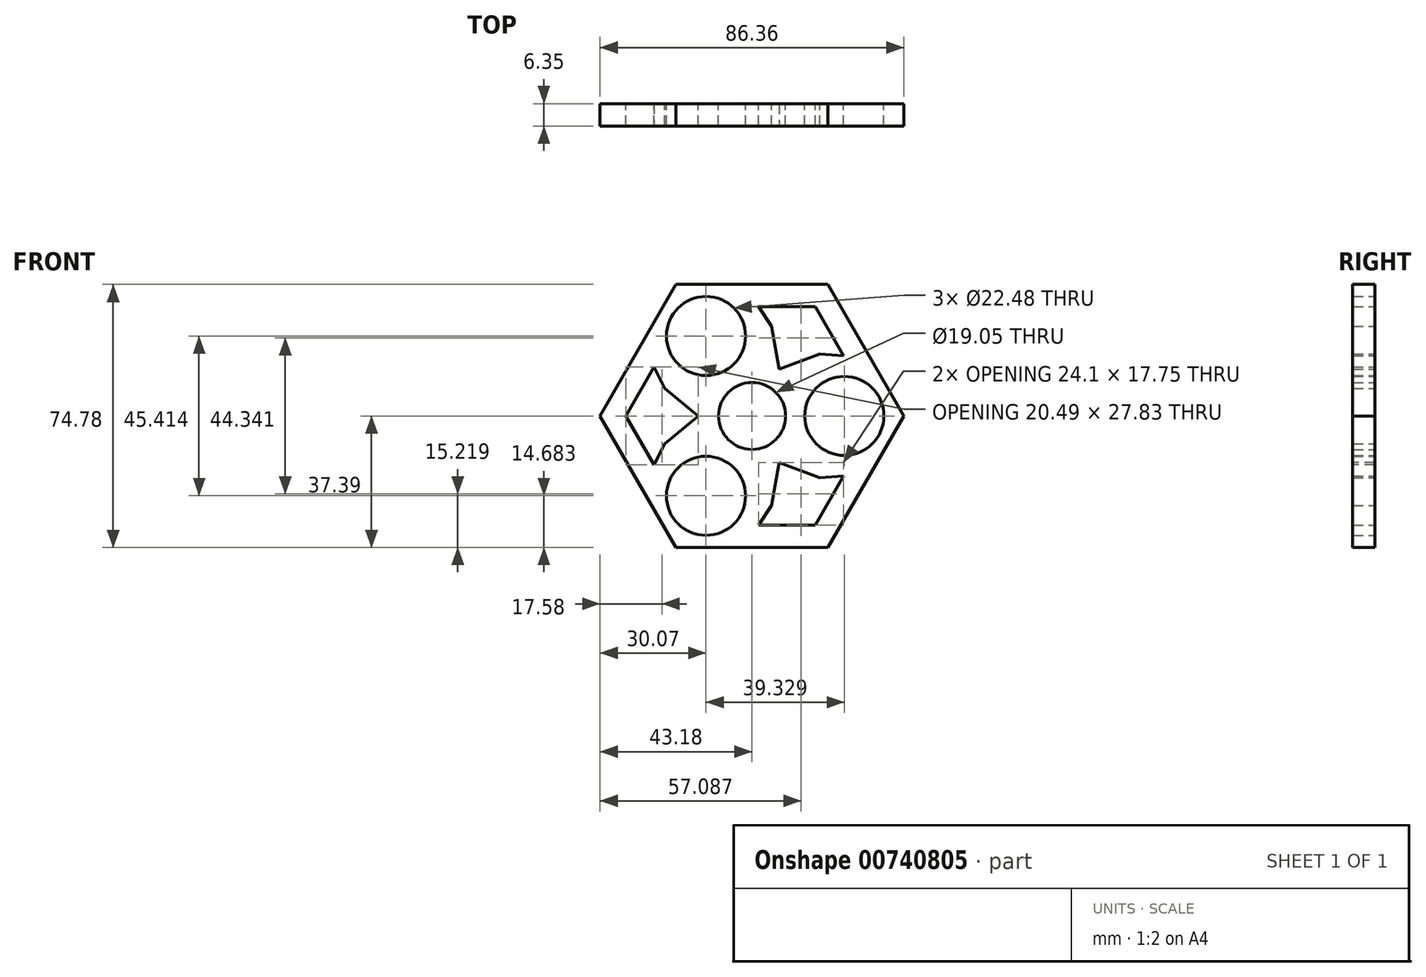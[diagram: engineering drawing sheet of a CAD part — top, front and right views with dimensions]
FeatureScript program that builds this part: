
annotation { "Feature Type Name" : "Feature", "Feature Type Description" : "" }
export const myFeature = defineFeature(function(context is Context, id is Id, definition is map)
    precondition{}
    {
        {
            var Q0;
            Q0=qCreatedBy(makeId("Front.planeOp"),FACE);
            var sketch = newSketch(context, id + "F0", { "sketchPlane" : qUnion([Q0])});
            skLineSegment(sketch, "E0.0", {"start": v(33.57, 16.65) * mm, "end": v(42.45, 1.27) * mm});
            skLineSegment(sketch, "E0.1", {"start": v(42.45, -1.27) * mm, "end": v(33.57, -16.65) * mm});
            skLineSegment(sketch, "E0.2", {"start": v(-2.36, -37.4) * mm, "end": v(-20.12, -37.4) * mm});
            skLineSegment(sketch, "E0.3", {"start": v(-22.32, -36.12) * mm, "end": v(-31.2, -20.75) * mm});
            skLineSegment(sketch, "E0.4", {"start": v(-31.2, 20.75) * mm, "end": v(-22.32, 36.12) * mm});
            skLineSegment(sketch, "E0.5", {"start": v(-20.12, 37.4) * mm, "end": v(-2.36, 37.4) * mm});
            skPoint(sketch, "E0.0.midPoint", {"position": v(32.38, 18.7) * mm});
            skPoint(sketch, "E1.visualSharp", {"position": v(-43.18, 0) * mm});
            skPoint(sketch, "E2.visualSharp", {"position": v(-21.59, 37.4) * mm});
            skArc(sketch, "E2.filletArc", {"start": v(-20.12, 37.4) * mm, "mid": v(-21.4, 37.05) * mm, "end": v(-22.32, 36.12) * mm});
            skPoint(sketch, "E3.visualSharp", {"position": v(21.6, 37.4) * mm});
            skPoint(sketch, "E4.visualSharp", {"position": v(43.18, 0) * mm});
            skArc(sketch, "E4.filletArc", {"start": v(42.45, -1.27) * mm, "mid": v(42.79, 0) * mm, "end": v(42.45, 1.27) * mm});
            skPoint(sketch, "E5.visualSharp", {"position": v(21.6, -37.4) * mm});
            skPoint(sketch, "E6.visualSharp", {"position": v(-21.59, -37.4) * mm});
            skArc(sketch, "E6.filletArc", {"start": v(-22.32, -36.12) * mm, "mid": v(-21.4, -37.05) * mm, "end": v(-20.12, -37.4) * mm});
            skCircle(sketch, "E7", {"center": v(0, 0) * mm, "radius": 9.53 * mm});
            skCircle(sketch, "E8", {"center": v(-13.1, -22.7) * mm, "radius": 11.24 * mm});
            skCircle(sketch, "E9.MirrorC", {"center": v(26.22, 0) * mm, "radius": 11.24 * mm});
            skCircle(sketch, "E10.MirrorC", {"center": v(-13.1, 22.7) * mm, "radius": 11.24 * mm});
            skLineSegment(sketch, "E11.trimOffspring", {"start": v(-21.4, -37.05) * mm, "end": v(-21.59, -37.4) * mm});
            skLineSegment(sketch, "E12", {"start": v(-2.36, -37.4) * mm, "end": v(-2.32, -37.32) * mm});
            skLineSegment(sketch, "E13", {"start": v(5.58, -25.44) * mm, "end": v(7.68, -13.3) * mm});
            skLineSegment(sketch, "E14.MirrorCS", {"start": v(19.24, -17.55) * mm, "end": v(7.68, -13.3) * mm});
            skLineSegment(sketch, "E15.MirrorCS", {"start": v(19.24, 17.55) * mm, "end": v(7.68, 13.3) * mm});
            skLineSegment(sketch, "E16.MirrorCS", {"start": v(33.57, 16.65) * mm, "end": v(33.48, 16.65) * mm});
            skLineSegment(sketch, "E17.MirrorCS", {"start": v(5.58, 25.44) * mm, "end": v(7.68, 13.3) * mm});
            skLineSegment(sketch, "E18.MirrorCS", {"start": v(33.57, -16.65) * mm, "end": v(42.45, -1.27) * mm});
            skPoint(sketch, "E19.MirrorP", {"position": v(21.59, -37.4) * mm});
            skPoint(sketch, "E20.MirrorCS.end.orphan", {"position": v(42.45, -73.52) * mm});
            skPoint(sketch, "E20.MirrorCS.start.orphan", {"position": v(22.32, -38.67) * mm});
            skPoint(sketch, "E21.MirrorCS.end.orphan", {"position": v(20.12, -37.4) * mm});
            skPoint(sketch, "E21.MirrorCS.start.orphan", {"position": v(0, -37.4) * mm});
            skPoint(sketch, "E22.orphan", {"position": v(22.32, -36.12) * mm});
            skLineSegment(sketch, "E23.MirrorCS", {"start": v(-24.82, -7.89) * mm, "end": v(-15.35, 0) * mm});
            skLineSegment(sketch, "E24.MirrorCS", {"start": v(-31.2, 20.75) * mm, "end": v(-31.16, 20.67) * mm});
            skLineSegment(sketch, "E25.MirrorCS", {"start": v(-31.2, -20.75) * mm, "end": v(-31.16, -20.67) * mm});
            skPoint(sketch, "E1.filletArc.end.orphan", {"position": v(-42.45, -1.27) * mm});
            skLineSegment(sketch, "E26", {"start": v(7.68, 13.3) * mm, "end": v(19.24, 17.55) * mm});
            skCircle(sketch, "E27.cCircle", {"center": v(0, 0) * mm, "radius": 37.4 * mm, "construction": true});
            skLineSegment(sketch, "E27.0", {"start": v(33.57, 16.65) * mm, "end": v(43.18, 0) * mm});
            skLineSegment(sketch, "E27.1", {"start": v(43.18, 0) * mm, "end": v(21.6, -37.4) * mm});
            skLineSegment(sketch, "E27.2", {"start": v(21.6, -37.4) * mm, "end": v(-21.59, -37.4) * mm});
            skLineSegment(sketch, "E27.3", {"start": v(-21.59, -37.4) * mm, "end": v(-43.18, 0) * mm});
            skLineSegment(sketch, "E27.4", {"start": v(-43.18, 0) * mm, "end": v(-21.6, 37.4) * mm});
            skLineSegment(sketch, "E27.5", {"start": v(-21.6, 37.4) * mm, "end": v(-2.36, 37.4) * mm});
            skLineSegment(sketch, "E28.trimOffspring", {"start": v(17.92, -31.04) * mm, "end": v(25.96, -17.13) * mm});
            skLineSegment(sketch, "E29.trimOffspring", {"start": v(17.92, -31.04) * mm, "end": v(1.86, -31.04) * mm});
            skPoint(sketch, "E30.MirrorCS.start.orphan", {"position": v(16.1, -34.22) * mm});
            skPoint(sketch, "E31.0.start.orphan", {"position": v(21.6, -31.04) * mm});
            skLineSegment(sketch, "E32.trimOffspring", {"start": v(1.86, -31.04) * mm, "end": v(5.58, -25.44) * mm});
            skLineSegment(sketch, "E33.trimOffspring", {"start": v(25.96, -17.13) * mm, "end": v(19.24, -17.55) * mm});
            skPoint(sketch, "E34.orphan", {"position": v(21.59, 37.4) * mm});
            skPoint(sketch, "E35.orphan", {"position": v(-31.05, -2.77) * mm});
            skPoint(sketch, "E36.orphan", {"position": v(-31.05, 2.77) * mm});
            skPoint(sketch, "E37.orphan", {"position": v(-23.02, 11.15) * mm});
            skPoint(sketch, "E38.orphan", {"position": v(-23.02, -11.15) * mm});
            skLineSegment(sketch, "E39.trimOffspring", {"start": v(-24.86, -7.96) * mm, "end": v(-24.82, -7.89) * mm});
            skLineSegment(sketch, "E40.MirrorCS", {"start": v(17.92, 31.04) * mm, "end": v(25.96, 17.13) * mm});
            skLineSegment(sketch, "E41.MirrorCS", {"start": v(17.92, 31.04) * mm, "end": v(1.86, 31.04) * mm});
            skLineSegment(sketch, "E42.MirrorCS", {"start": v(21.6, 37.4) * mm, "end": v(-21.59, 37.4) * mm});
            skLineSegment(sketch, "E43.MirrorCS", {"start": v(43.18, 0) * mm, "end": v(21.6, 37.4) * mm});
            skLineSegment(sketch, "E44.trimOffspring", {"start": v(1.86, 31.04) * mm, "end": v(5.58, 25.44) * mm});
            skLineSegment(sketch, "E45.trimOffspring", {"start": v(25.96, 17.13) * mm, "end": v(19.24, 17.55) * mm});
            skLineSegment(sketch, "E46.MirrorCS", {"start": v(-35.85, 0) * mm, "end": v(-27.81, -13.92) * mm});
            skLineSegment(sketch, "E47.MirrorCS", {"start": v(-35.85, 0) * mm, "end": v(-27.81, 13.92) * mm});
            skLineSegment(sketch, "E48.MirrorCS", {"start": v(-27.81, 13.92) * mm, "end": v(-24.82, 7.89) * mm});
            skLineSegment(sketch, "E49.MirrorCS", {"start": v(-27.81, -13.92) * mm, "end": v(-24.86, -7.96) * mm});
            skLineSegment(sketch, "E50", {"start": v(-24.82, 7.89) * mm, "end": v(-15.35, 0) * mm});
            skSolve(sketch);
        }
        {
            var Q0;
            Q0=qSketchRegion(id+"F0",true);
            extrude(context, id + "F1", {"entities" : qUnion([Q0]), "depth" : 6.35 * mm, "offsetDistance" : 25.4 * mm});
        }
    });
